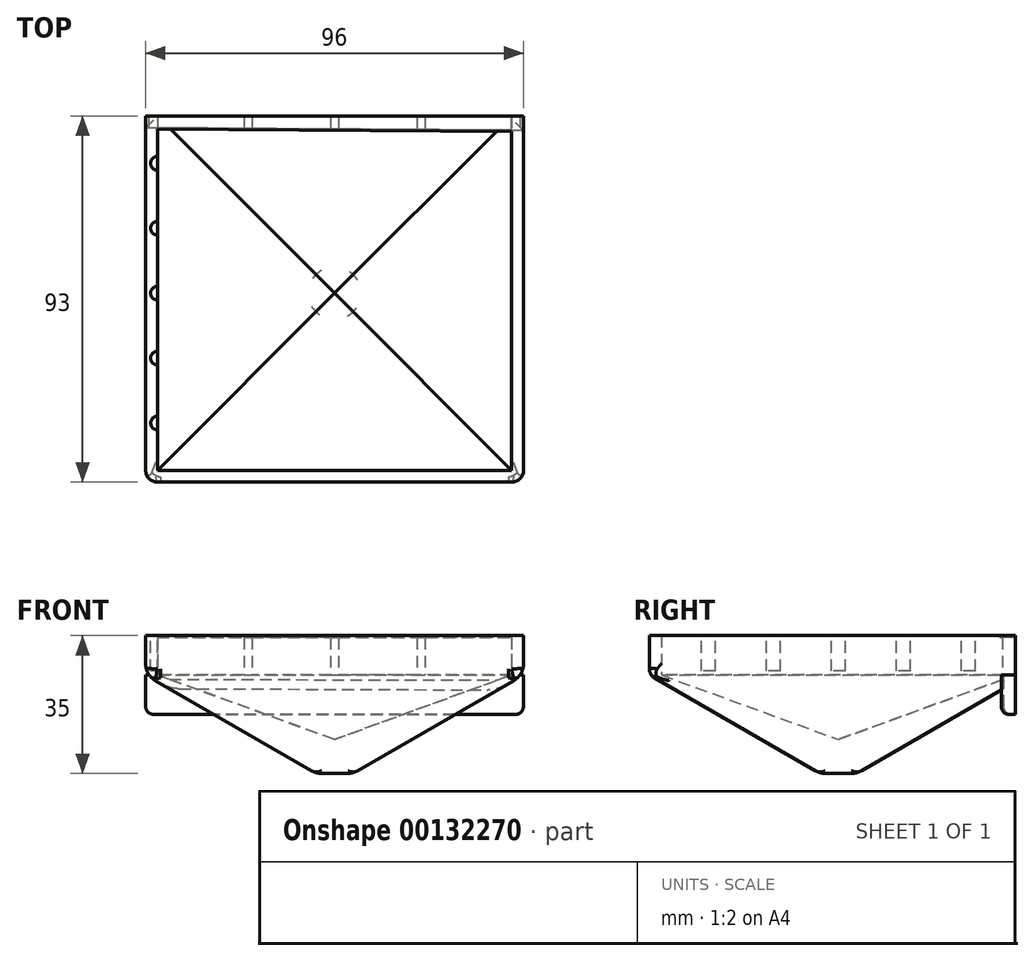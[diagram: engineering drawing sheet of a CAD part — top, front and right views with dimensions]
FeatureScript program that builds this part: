
annotation { "Feature Type Name" : "Feature", "Feature Type Description" : "" }
export const myFeature = defineFeature(function(context is Context, id is Id, definition is map)
    precondition{}
    {
        {
            var Q0;
            Q0=qCreatedBy(makeId("Top.planeOp"),FACE);
            var sketch = newSketch(context, id + "F0", { "sketchPlane" : qUnion([Q0])});
            skLineSegment(sketch, "E0.bottom", {"start": v(-45, 45) * mm, "end": v(45, 45) * mm});
            skLineSegment(sketch, "E0.top", {"start": v(-45, -45) * mm, "end": v(45, -45) * mm});
            skLineSegment(sketch, "E0.left", {"start": v(-45, 45) * mm, "end": v(-45, -45) * mm});
            skLineSegment(sketch, "E0.right", {"start": v(45, 45) * mm, "end": v(45, -45) * mm});
            skLineSegment(sketch, "E1.0", {"start": v(-48, 48) * mm, "end": v(48, 48) * mm});
            skLineSegment(sketch, "E1.1", {"start": v(-48, 48) * mm, "end": v(-48, -48) * mm});
            skLineSegment(sketch, "E1.2", {"start": v(-48, -48) * mm, "end": v(48, -48) * mm});
            skLineSegment(sketch, "E1.3", {"start": v(48, 48) * mm, "end": v(48, -48) * mm});
            skSolve(sketch);
        }
        {
            var Q0;
            Q0=makeQuery(id+"F0.imprint","IMPRINT",FACE,{"disambiguationData":[TD([[makeQuery(id+"F0.imprint","IMPRINT",EDGE,{"derivedFrom":sQuery(id+"F0.wireOp",EDGE,"E0.bottom")}),1.0]])]});
            var Q1;
            Q1=makeQuery(id+"F0.imprint","IMPRINT",FACE,{"disambiguationData":[TD([[makeQuery(id+"F0.imprint","IMPRINT",EDGE,{"derivedFrom":sQuery(id+"F0.wireOp",EDGE,"E0.bottom")}),-1.0]])]});
            extrude(context, id + "F1", {"entities" : qUnion([Q0, Q1]), "oppositeDirection" : true, "depth" : 25 * mm, "hasDraft" : true, "draftAngle" : 60 * degree, "draftPullDirection" : true});
        }
        {
            var Q0;
            Q0=makeQuery(id+"F0.imprint","IMPRINT",FACE,{"disambiguationData":[TD([[makeQuery(id+"F0.imprint","IMPRINT",EDGE,{"derivedFrom":sQuery(id+"F0.wireOp",EDGE,"E0.bottom")}),-1.0]])]});
            extrude(context, id + "F2", {"entities" : qUnion([Q0]), "operationType" : NewBodyOperationType.REMOVE, "oppositeDirection" : true, "depth" : 25 * mm, "hasDraft" : true, "draftAngle" : 70 * degree, "draftPullDirection" : true});
        }
        {
            var Q0;
            Q0=makeQuery(id+"F0.imprint","IMPRINT",FACE,{"disambiguationData":[TD([[makeQuery(id+"F0.imprint","IMPRINT",EDGE,{"derivedFrom":sQuery(id+"F0.wireOp",EDGE,"E0.bottom")}),1.0]])]});
            extrude(context, id + "F3", {"entities" : qUnion([Q0]), "operationType" : NewBodyOperationType.ADD, "depth" : 10 * mm});
        }
        {
            var Q0;
            Q0=makeQuery(id+"F3.opExtrude","CAP_FACE",FACE,{"disambiguationData":[OSD([sQuery(id+"F0.wireOp",EDGE,"E0.bottom"),sQuery(id+"F0.wireOp",EDGE,"E0.top"),sQuery(id+"F0.wireOp",EDGE,"E0.left"),sQuery(id+"F0.wireOp",EDGE,"E0.right"),sQuery(id+"F0.wireOp",EDGE,"E1.0"),sQuery(id+"F0.wireOp",EDGE,"E1.1"),sQuery(id+"F0.wireOp",EDGE,"E1.2"),sQuery(id+"F0.wireOp",EDGE,"E1.3")])],"isStart":false});
            var sketch = newSketch(context, id + "F4", { "sketchPlane" : qUnion([Q0])});
            skCircle(sketch, "E2", {"center": v(-45, 33.02) * mm, "radius": 1.75 * mm});
            skCircle(sketch, "E3.1.0.0", {"center": v(-44.99, 16.52) * mm, "radius": 1.75 * mm});
            skCircle(sketch, "E3.2.0.0", {"center": v(-44.97, 0.02) * mm, "radius": 1.75 * mm});
            skCircle(sketch, "E3.3.0.0", {"center": v(-44.96, -16.48) * mm, "radius": 1.75 * mm});
            skCircle(sketch, "E3.4.0.0", {"center": v(-44.95, -32.98) * mm, "radius": 1.75 * mm});
            skLineSegment(sketch, "E3.direction1", {"start": v(-45, 33.02) * mm, "end": v(-44.99, 16.52) * mm, "construction": true});
            skLineSegment(sketch, "E4.MirrorCS", {"start": v(45, 33.02) * mm, "end": v(44.99, 16.52) * mm, "construction": true});
            skCircle(sketch, "E5.MirrorC", {"center": v(44.95, -32.98) * mm, "radius": 1.75 * mm});
            skCircle(sketch, "E6.MirrorC", {"center": v(44.97, 0.02) * mm, "radius": 1.75 * mm});
            skCircle(sketch, "E7.MirrorC", {"center": v(44.96, -16.48) * mm, "radius": 1.75 * mm});
            skCircle(sketch, "E8.MirrorC", {"center": v(44.99, 16.52) * mm, "radius": 1.75 * mm});
            skCircle(sketch, "E9.MirrorC", {"center": v(45, 33.02) * mm, "radius": 1.75 * mm});
            skSolve(sketch);
        }
        {
            var Q0;
            {var subQ0=sQuery(id+"F4.wireOp",EDGE,"E2");var subQ1=makeQuery(id+"F3.opExtrude","CAP_EDGE",EDGE,{"disambiguationData":[OSD([sQuery(id+"F0.wireOp",EDGE,"E0.left")])],"isStart":false});var subQ2=makeQuery(id+"F4.imprint","INTERSECT",VERTEX,{"disambiguationData":[OD(0.0)],"derivedFrom":[subQ1,subQ0]});Q0=makeQuery(id+"F4.imprint","IMPRINT",FACE,{"disambiguationData":[TD([[makeQuery(id+"F4.imprint","IMPRINT",EDGE,{"disambiguationData":[TD([[subQ2,-1.0]])],"derivedFrom":subQ0}),1.0]])]});}
            var Q1;
            {var subQ0=sQuery(id+"F4.wireOp",EDGE,"E3.1.0.0");var subQ1=makeQuery(id+"F3.opExtrude","CAP_EDGE",EDGE,{"disambiguationData":[OSD([sQuery(id+"F0.wireOp",EDGE,"E0.left")])],"isStart":false});var subQ2=makeQuery(id+"F4.imprint","INTERSECT",VERTEX,{"disambiguationData":[OD(0.0)],"derivedFrom":[subQ1,subQ0]});Q1=makeQuery(id+"F4.imprint","IMPRINT",FACE,{"disambiguationData":[TD([[makeQuery(id+"F4.imprint","IMPRINT",EDGE,{"disambiguationData":[TD([[subQ2,-1.0]])],"derivedFrom":subQ0}),1.0]])]});}
            var Q2;
            {var subQ0=sQuery(id+"F4.wireOp",EDGE,"E3.2.0.0");var subQ1=makeQuery(id+"F3.opExtrude","CAP_EDGE",EDGE,{"disambiguationData":[OSD([sQuery(id+"F0.wireOp",EDGE,"E0.left")])],"isStart":false});var subQ2=makeQuery(id+"F4.imprint","INTERSECT",VERTEX,{"disambiguationData":[OD(0.0)],"derivedFrom":[subQ1,subQ0]});Q2=makeQuery(id+"F4.imprint","IMPRINT",FACE,{"disambiguationData":[TD([[makeQuery(id+"F4.imprint","IMPRINT",EDGE,{"disambiguationData":[TD([[subQ2,-1.0]])],"derivedFrom":subQ0}),1.0]])]});}
            var Q3;
            {var subQ0=sQuery(id+"F4.wireOp",EDGE,"E3.3.0.0");var subQ1=makeQuery(id+"F3.opExtrude","CAP_EDGE",EDGE,{"disambiguationData":[OSD([sQuery(id+"F0.wireOp",EDGE,"E0.left")])],"isStart":false});var subQ2=makeQuery(id+"F4.imprint","INTERSECT",VERTEX,{"disambiguationData":[OD(0.0)],"derivedFrom":[subQ1,subQ0]});Q3=makeQuery(id+"F4.imprint","IMPRINT",FACE,{"disambiguationData":[TD([[makeQuery(id+"F4.imprint","IMPRINT",EDGE,{"disambiguationData":[TD([[subQ2,1.0]])],"derivedFrom":subQ0}),1.0]])]});}
            var Q4;
            {var subQ0=sQuery(id+"F4.wireOp",EDGE,"E3.4.0.0");var subQ1=makeQuery(id+"F3.opExtrude","CAP_EDGE",EDGE,{"disambiguationData":[OSD([sQuery(id+"F0.wireOp",EDGE,"E0.left")])],"isStart":false});var subQ2=makeQuery(id+"F4.imprint","INTERSECT",VERTEX,{"disambiguationData":[OD(0.0)],"derivedFrom":[subQ1,subQ0]});Q4=makeQuery(id+"F4.imprint","IMPRINT",FACE,{"disambiguationData":[TD([[makeQuery(id+"F4.imprint","IMPRINT",EDGE,{"disambiguationData":[TD([[subQ2,1.0]])],"derivedFrom":subQ0}),1.0]])]});}
            var Q5;
            {var subQ0=sQuery(id+"F4.wireOp",EDGE,"E5.MirrorC");var subQ1=makeQuery(id+"F3.opExtrude","CAP_EDGE",EDGE,{"disambiguationData":[OSD([sQuery(id+"F0.wireOp",EDGE,"E0.right")])],"isStart":false});var subQ2=makeQuery(id+"F4.imprint","INTERSECT",VERTEX,{"disambiguationData":[OD(0.0)],"derivedFrom":[subQ1,subQ0]});Q5=makeQuery(id+"F4.imprint","IMPRINT",FACE,{"disambiguationData":[TD([[makeQuery(id+"F4.imprint","IMPRINT",EDGE,{"disambiguationData":[TD([[subQ2,1.0]])],"derivedFrom":subQ0}),-1.0]])]});}
            var Q6;
            {var subQ0=sQuery(id+"F4.wireOp",EDGE,"E7.MirrorC");var subQ1=makeQuery(id+"F3.opExtrude","CAP_EDGE",EDGE,{"disambiguationData":[OSD([sQuery(id+"F0.wireOp",EDGE,"E0.right")])],"isStart":false});var subQ2=makeQuery(id+"F4.imprint","INTERSECT",VERTEX,{"disambiguationData":[OD(0.0)],"derivedFrom":[subQ1,subQ0]});Q6=makeQuery(id+"F4.imprint","IMPRINT",FACE,{"disambiguationData":[TD([[makeQuery(id+"F4.imprint","IMPRINT",EDGE,{"disambiguationData":[TD([[subQ2,1.0]])],"derivedFrom":subQ0}),-1.0]])]});}
            var Q7;
            {var subQ0=sQuery(id+"F4.wireOp",EDGE,"E6.MirrorC");var subQ1=makeQuery(id+"F3.opExtrude","CAP_EDGE",EDGE,{"disambiguationData":[OSD([sQuery(id+"F0.wireOp",EDGE,"E0.right")])],"isStart":false});var subQ2=makeQuery(id+"F4.imprint","INTERSECT",VERTEX,{"disambiguationData":[OD(0.0)],"derivedFrom":[subQ1,subQ0]});Q7=makeQuery(id+"F4.imprint","IMPRINT",FACE,{"disambiguationData":[TD([[makeQuery(id+"F4.imprint","IMPRINT",EDGE,{"disambiguationData":[TD([[subQ2,1.0]])],"derivedFrom":subQ0}),-1.0]])]});}
            var Q8;
            {var subQ0=sQuery(id+"F4.wireOp",EDGE,"E8.MirrorC");var subQ1=makeQuery(id+"F3.opExtrude","CAP_EDGE",EDGE,{"disambiguationData":[OSD([sQuery(id+"F0.wireOp",EDGE,"E0.right")])],"isStart":false});var subQ2=makeQuery(id+"F4.imprint","INTERSECT",VERTEX,{"disambiguationData":[OD(0.0)],"derivedFrom":[subQ1,subQ0]});Q8=makeQuery(id+"F4.imprint","IMPRINT",FACE,{"disambiguationData":[TD([[makeQuery(id+"F4.imprint","IMPRINT",EDGE,{"disambiguationData":[TD([[subQ2,-1.0]])],"derivedFrom":subQ0}),-1.0]])]});}
            var Q9;
            {var subQ0=sQuery(id+"F4.wireOp",EDGE,"E9.MirrorC");var subQ1=makeQuery(id+"F3.opExtrude","CAP_EDGE",EDGE,{"disambiguationData":[OSD([sQuery(id+"F0.wireOp",EDGE,"E0.right")])],"isStart":false});var subQ2=makeQuery(id+"F4.imprint","INTERSECT",VERTEX,{"disambiguationData":[OD(0.0)],"derivedFrom":[subQ1,subQ0]});Q9=makeQuery(id+"F4.imprint","IMPRINT",FACE,{"disambiguationData":[TD([[makeQuery(id+"F4.imprint","IMPRINT",EDGE,{"disambiguationData":[TD([[subQ2,-1.0]])],"derivedFrom":subQ0}),-1.0]])]});}
            extrude(context, id + "F5", {"entities" : qUnion([Q0, Q1, Q2, Q3, Q4, Q5, Q6, Q7, Q8, Q9]), "operationType" : NewBodyOperationType.REMOVE, "oppositeDirection" : true, "depth" : 9 * mm});
        }
        {
            var Q0;
            Q0=makeQuery(id+"F1.opExtrude","SWEPT_FACE",FACE,{"disambiguationData":[OSD([sQuery(id+"F0.wireOp",EDGE,"E1.3")])]});
            var Q1;
            Q1=makeQuery(id+"F1.opExtrude","SWEPT_FACE",FACE,{"disambiguationData":[OSD([sQuery(id+"F0.wireOp",EDGE,"E1.1")])]});
            fillet(context, id + "F6", {"entities" : qUnion([Q0, Q1]), "radius" : 5 * mm, "tangentPropagation" : true, "allowEdgeOverflow" : false});
        }
        {
            var Q0;
            Q0=makeQuery(id+"F3.opExtrude","SWEPT_EDGE",EDGE,{"disambiguationData":[OSD([sQuery(id+"F0.wireOp",EDGE,"E1.1"),sQuery(id+"F0.wireOp",EDGE,"E1.2")])]});
            var Q1;
            Q1=makeQuery(id+"F3.opExtrude","SWEPT_EDGE",EDGE,{"disambiguationData":[OSD([sQuery(id+"F0.wireOp",EDGE,"E1.0"),sQuery(id+"F0.wireOp",EDGE,"E1.1")])]});
            var Q2;
            Q2=makeQuery(id+"F3.opExtrude","SWEPT_EDGE",EDGE,{"disambiguationData":[OSD([sQuery(id+"F0.wireOp",EDGE,"E1.0"),sQuery(id+"F0.wireOp",EDGE,"E1.3")])]});
            var Q3;
            Q3=makeQuery(id+"F3.opExtrude","SWEPT_EDGE",EDGE,{"disambiguationData":[OSD([sQuery(id+"F0.wireOp",EDGE,"E1.2"),sQuery(id+"F0.wireOp",EDGE,"E1.3")])]});
            fillet(context, id + "F7", {"entities" : qUnion([Q0, Q1, Q2, Q3]), "radius" : 3 * mm, "tangentPropagation" : true, "allowEdgeOverflow" : false});
        }
        {
            var Q0;
            Q0=makeQuery(id+"F1.opExtrude","CAP_FACE",FACE,{"disambiguationData":[OSD([sQuery(id+"F0.wireOp",EDGE,"E1.0"),sQuery(id+"F0.wireOp",EDGE,"E1.1"),sQuery(id+"F0.wireOp",EDGE,"E1.2"),sQuery(id+"F0.wireOp",EDGE,"E1.3")])],"isStart":false});
            fillet(context, id + "F8", {"entities" : qUnion([Q0]), "radius" : 5 * mm, "tangentPropagation" : true, "allowEdgeOverflow" : false});
        }
        {
            var Q0;
            {var subQ0=sQuery(id+"F0.wireOp",EDGE,"E1.2");Q0=makeQuery(id+"F3.boolean.opBoolean","MERGE",EDGE,{"derivedFrom":[makeQuery(id+"F1.opExtrude","CAP_EDGE",EDGE,{"disambiguationData":[OSD([subQ0])],"isStart":true}),makeQuery(id+"F3.opExtrude","CAP_EDGE",EDGE,{"disambiguationData":[OSD([subQ0])],"isStart":true})]});}
            var Q1;
            {var subQ0=sQuery(id+"F0.wireOp",EDGE,"E1.0");Q1=makeQuery(id+"F3.boolean.opBoolean","MERGE",EDGE,{"derivedFrom":[makeQuery(id+"F1.opExtrude","CAP_EDGE",EDGE,{"disambiguationData":[OSD([subQ0])],"isStart":true}),makeQuery(id+"F3.opExtrude","CAP_EDGE",EDGE,{"disambiguationData":[OSD([subQ0])],"isStart":true})]});}
            fillet(context, id + "F9", {"entities" : qUnion([Q0, Q1]), "radius" : 2.6 * mm, "tangentPropagation" : true, "allowEdgeOverflow" : false});
        }
        {
            var Q0;
            Q0=makeQuery(id+"F3.opExtrude","CAP_FACE",FACE,{"disambiguationData":[OSD([sQuery(id+"F0.wireOp",EDGE,"E0.bottom"),sQuery(id+"F0.wireOp",EDGE,"E0.top"),sQuery(id+"F0.wireOp",EDGE,"E0.left"),sQuery(id+"F0.wireOp",EDGE,"E0.right"),sQuery(id+"F0.wireOp",EDGE,"E1.0"),sQuery(id+"F0.wireOp",EDGE,"E1.1"),sQuery(id+"F0.wireOp",EDGE,"E1.2"),sQuery(id+"F0.wireOp",EDGE,"E1.3")])],"isStart":false});
            var sketch = newSketch(context, id + "F10", { "sketchPlane" : qUnion([Q0])});
            skLineSegment(sketch, "E10", {"start": v(-48, 45) * mm, "end": v(48, 45) * mm});
            skLineSegment(sketch, "E11", {"start": v(48, 45) * mm, "end": v(48, 49.86) * mm});
            skLineSegment(sketch, "E12", {"start": v(48, 49.86) * mm, "end": v(-48, 49.86) * mm});
            skLineSegment(sketch, "E13", {"start": v(-48, 49.86) * mm, "end": v(-48, 45) * mm});
            skSolve(sketch);
        }
        {
            var Q0;
            Q0 = qSketchRegion(id + "F10", true);
            extrude(context, id + "F11", {"entities" : qUnion([Q0]), "operationType" : NewBodyOperationType.REMOVE, "oppositeDirection" : true, "depth" : 25 * mm});
        }
        {
            var Q0;
            Q0=makeQuery(id+"F3.opExtrude","CAP_FACE",FACE,{"disambiguationData":[OSD([sQuery(id+"F0.wireOp",EDGE,"E0.bottom"),sQuery(id+"F0.wireOp",EDGE,"E0.top"),sQuery(id+"F0.wireOp",EDGE,"E0.left"),sQuery(id+"F0.wireOp",EDGE,"E0.right"),sQuery(id+"F0.wireOp",EDGE,"E1.0"),sQuery(id+"F0.wireOp",EDGE,"E1.1"),sQuery(id+"F0.wireOp",EDGE,"E1.2"),sQuery(id+"F0.wireOp",EDGE,"E1.3")])],"isStart":false});
            var sketch = newSketch(context, id + "F12", { "sketchPlane" : qUnion([Q0])});
            skLineSegment(sketch, "E14", {"start": v(-48, 45) * mm, "end": v(48, 45) * mm});
            skLineSegment(sketch, "E15", {"start": v(48, 45) * mm, "end": v(47.98, 41.37) * mm});
            skLineSegment(sketch, "E16", {"start": v(47.98, 41.37) * mm, "end": v(-48, 42) * mm});
            skLineSegment(sketch, "E17", {"start": v(-48, 42) * mm, "end": v(-48, 45) * mm});
            skSolve(sketch);
        }
        {
            var Q0;
            Q0 = qSketchRegion(id + "F12", true);
            extrude(context, id + "F13", {"entities" : qUnion([Q0]), "operationType" : NewBodyOperationType.ADD, "oppositeDirection" : true, "depth" : 20 * mm, "hasSecondDirection" : true, "secondDirectionOppositeDirection" : true, "secondDirectionDepth" : 10 * mm});
        }
        {
            var Q0;
            Q0=makeQuery(id+"F13.opExtrude","CAP_EDGE",EDGE,{"disambiguationData":[OSD([sQuery(id+"F12.wireOp",EDGE,"E17")])],"isStart":false});
            var Q1;
            Q1=makeQuery(id+"F13.opExtrude","CAP_EDGE",EDGE,{"disambiguationData":[OSD([sQuery(id+"F12.wireOp",EDGE,"E15")])],"isStart":false});
            var Q2;
            Q2=makeQuery(id+"F13.opExtrude","CAP_EDGE",EDGE,{"disambiguationData":[OSD([sQuery(id+"F12.wireOp",EDGE,"E16")])],"isStart":false});
            fillet(context, id + "F14", {"entities" : qUnion([Q0, Q1, Q2]), "radius" : 2 * mm, "tangentPropagation" : true, "allowEdgeOverflow" : false});
        }
        {
            var Q0;
            {var subQ1=sQuery(id+"F0.wireOp",EDGE,"E0.left");var subQ2=sQuery(id+"F12.wireOp",EDGE,"E14");var subQ3=sQuery(id+"F12.wireOp",EDGE,"E16");Q0=makeQuery(id+"F13.boolean.opBoolean","SPLIT",FACE,{"disambiguationData":[TD([makeQuery(id+"F2.boolean.opBoolean","COPY",FACE,{"derivedFrom":makeQuery(id+"F2.opExtrude","SWEPT_FACE",FACE,{"disambiguationData":[OSD([subQ1])]})})])],"derivedFrom":makeQuery(id+"F13.opExtrude","CAP_FACE",FACE,{"disambiguationData":[OSD([subQ2,sQuery(id+"F12.wireOp",EDGE,"E15"),subQ3,sQuery(id+"F12.wireOp",EDGE,"E17")])],"isStart":true})});}
            var sketch = newSketch(context, id + "F15", { "sketchPlane" : qUnion([Q0])});
            skLineSegment(sketch, "E18.bottom", {"start": v(-1, 45) * mm, "end": v(1, 45) * mm});
            skLineSegment(sketch, "E18.top", {"start": v(-1, 41.68) * mm, "end": v(1, 41.68) * mm});
            skLineSegment(sketch, "E18.left", {"start": v(-1, 45) * mm, "end": v(-1, 41.68) * mm});
            skLineSegment(sketch, "E18.right", {"start": v(1, 45) * mm, "end": v(1, 41.68) * mm});
            skLineSegment(sketch, "E19.1.0.0", {"start": v(-23, 45) * mm, "end": v(-23, 41.68) * mm});
            skLineSegment(sketch, "E19.1.0.1", {"start": v(-21, 45) * mm, "end": v(-21, 41.68) * mm});
            skLineSegment(sketch, "E19.1.0.2", {"start": v(-23, 45) * mm, "end": v(-21, 45) * mm});
            skLineSegment(sketch, "E19.1.0.3", {"start": v(-23, 41.68) * mm, "end": v(-21, 41.68) * mm});
            skLineSegment(sketch, "E19.direction1", {"start": v(-1, 41.68) * mm, "end": v(-23, 41.68) * mm, "construction": true});
            skLineSegment(sketch, "E20.1.0.0", {"start": v(21, 45) * mm, "end": v(23, 45) * mm});
            skLineSegment(sketch, "E20.1.0.1", {"start": v(23, 45) * mm, "end": v(23, 41.68) * mm});
            skLineSegment(sketch, "E20.1.0.2", {"start": v(21, 41.68) * mm, "end": v(23, 41.68) * mm});
            skLineSegment(sketch, "E20.1.0.3", {"start": v(21, 45) * mm, "end": v(21, 41.68) * mm});
            skLineSegment(sketch, "E20.direction1", {"start": v(-1, 45) * mm, "end": v(21, 45) * mm, "construction": true});
            skSolve(sketch);
        }
        {
            var Q0;
            Q0 = qSketchRegion(id + "F15", true);
            var Q1;
            Q1=makeQuery(id+"F3.opExtrude","CAP_FACE",FACE,{"disambiguationData":[OSD([sQuery(id+"F0.wireOp",EDGE,"E0.bottom"),sQuery(id+"F0.wireOp",EDGE,"E0.top"),sQuery(id+"F0.wireOp",EDGE,"E0.left"),sQuery(id+"F0.wireOp",EDGE,"E0.right"),sQuery(id+"F0.wireOp",EDGE,"E1.0"),sQuery(id+"F0.wireOp",EDGE,"E1.1"),sQuery(id+"F0.wireOp",EDGE,"E1.2"),sQuery(id+"F0.wireOp",EDGE,"E1.3")])],"isStart":false});
            extrude(context, id + "F16", {"entities" : qUnion([Q0]), "operationType" : NewBodyOperationType.ADD, "endBound" : BoundingType.UP_TO_SURFACE, "endBoundEntityFace" : qUnion([Q1]), "depth" : 25 * mm});
        }
        {
            var Q0;
            Q0=makeQuery(id+"F3.opExtrude","CAP_FACE",FACE,{"disambiguationData":[OSD([sQuery(id+"F0.wireOp",EDGE,"E0.bottom"),sQuery(id+"F0.wireOp",EDGE,"E0.top"),sQuery(id+"F0.wireOp",EDGE,"E0.left"),sQuery(id+"F0.wireOp",EDGE,"E0.right"),sQuery(id+"F0.wireOp",EDGE,"E1.0"),sQuery(id+"F0.wireOp",EDGE,"E1.1"),sQuery(id+"F0.wireOp",EDGE,"E1.2"),sQuery(id+"F0.wireOp",EDGE,"E1.3")])],"isStart":false});
            var sketch = newSketch(context, id + "F17", { "sketchPlane" : qUnion([Q0])});
            skLineSegment(sketch, "E21", {"start": v(-45, 45) * mm, "end": v(45, 45) * mm});
            skLineSegment(sketch, "E22", {"start": v(45, 45) * mm, "end": v(45, 41.09) * mm});
            skLineSegment(sketch, "E23", {"start": v(45, 41.09) * mm, "end": v(-45, 41.7) * mm});
            skLineSegment(sketch, "E24", {"start": v(-45, 41.7) * mm, "end": v(-45, 45) * mm});
            skSolve(sketch);
        }
        {
            var Q0;
            Q0=makeQuery(id+"F17.imprint","IMPRINT",FACE,{"disambiguationData":[TD([[makeQuery(id+"F17.imprint","IMPRINT",EDGE,{"derivedFrom":sQuery(id+"F17.wireOp",EDGE,"E21")}),-1.0]])]});
            extrude(context, id + "F18", {"entities" : qUnion([Q0]), "operationType" : NewBodyOperationType.ADD, "oppositeDirection" : true, "depth" : .5 * mm});
        }
    });
